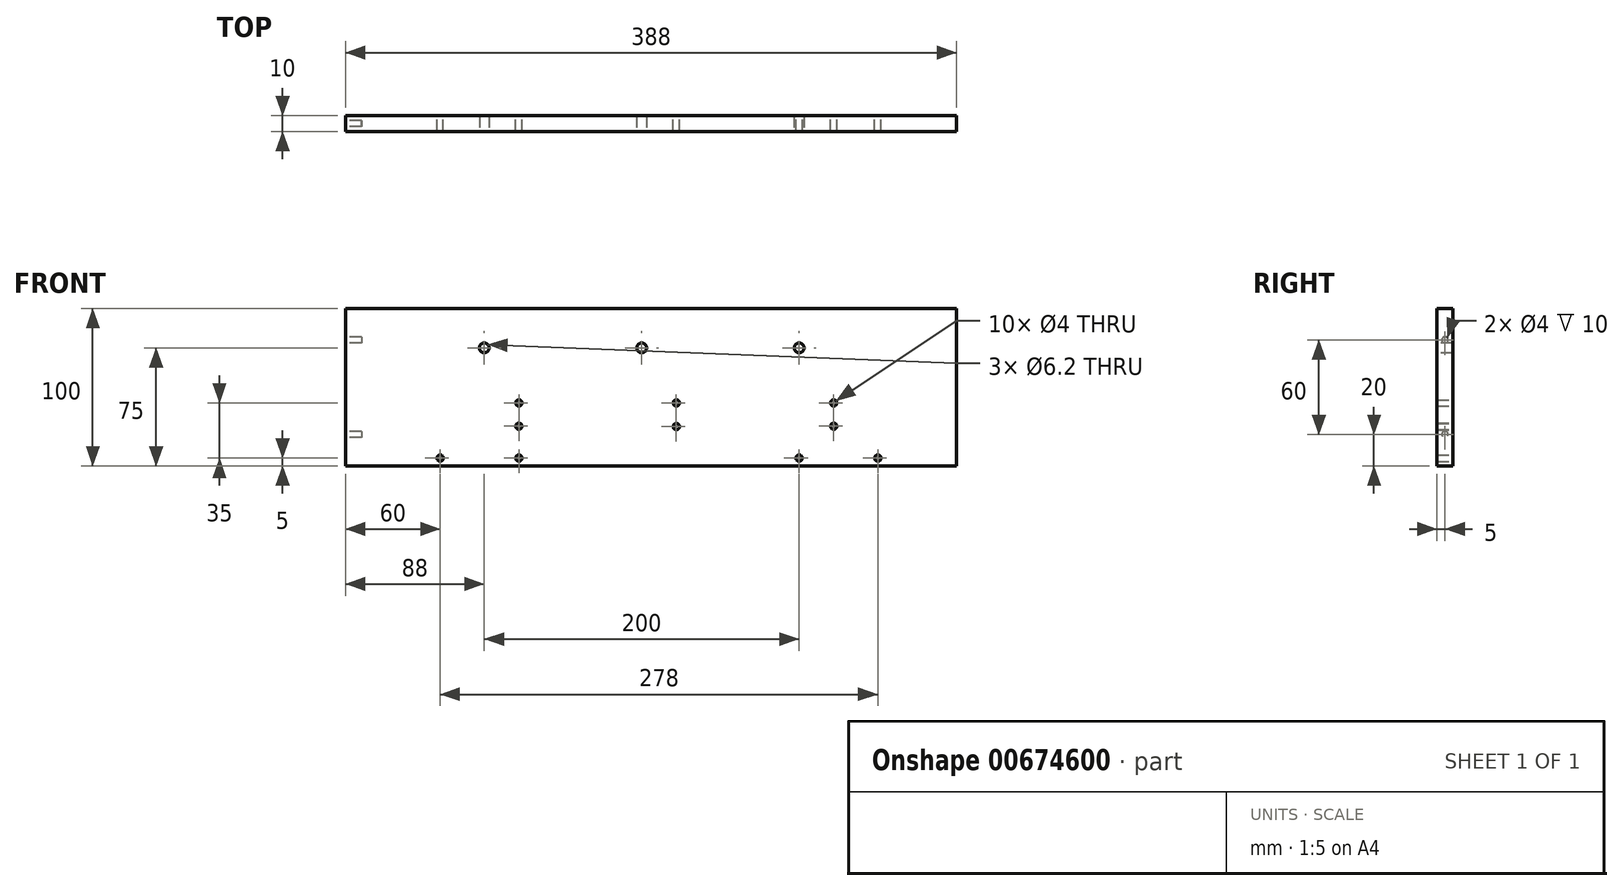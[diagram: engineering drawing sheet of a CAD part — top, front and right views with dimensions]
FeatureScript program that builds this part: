
annotation { "Feature Type Name" : "Feature", "Feature Type Description" : "" }
export const myFeature = defineFeature(function(context is Context, id is Id, definition is map)
    precondition{}
    {
        {
            var Q0;
            Q0=qCreatedBy(makeId("Front.planeOp"),FACE);
            var sketch = newSketch(context, id + "F0", { "sketchPlane" : qUnion([Q0])});
            skLineSegment(sketch, "E0.bottom", {"start": v(194, 50) * mm, "end": v(-194, 50) * mm});
            skLineSegment(sketch, "E0.top", {"start": v(194, -50) * mm, "end": v(-194, -50) * mm});
            skLineSegment(sketch, "E0.left", {"start": v(194, 50) * mm, "end": v(194, -50) * mm});
            skLineSegment(sketch, "E0.right", {"start": v(-194, 50) * mm, "end": v(-194, -50) * mm});
            skPoint(sketch, "E0.middle", {"position": v(0, 0) * mm});
            skCircle(sketch, "E1", {"center": v(144, -45) * mm, "radius": 2 * mm});
            skCircle(sketch, "E2", {"center": v(-134, -45) * mm, "radius": 2 * mm});
            skPoint(sketch, "E3", {"position": v(0, -45) * mm});
            skCircle(sketch, "E4", {"center": v(116, -10) * mm, "radius": 2 * mm});
            skCircle(sketch, "E5", {"center": v(16, -10) * mm, "radius": 2 * mm});
            skCircle(sketch, "E6", {"center": v(-84, -10) * mm, "radius": 2 * mm});
            skLineSegment(sketch, "E7", {"start": v(-84, -10) * mm, "end": v(16, -10) * mm, "construction": true});
            skLineSegment(sketch, "E8", {"start": v(116, -10) * mm, "end": v(16, -10) * mm, "construction": true});
            skCircle(sketch, "E9", {"center": v(-84, -45) * mm, "radius": 2 * mm});
            skCircle(sketch, "E10", {"center": v(94, -45) * mm, "radius": 2 * mm});
            skCircle(sketch, "E11", {"center": v(116, -24.75) * mm, "radius": 2 * mm});
            skCircle(sketch, "E12", {"center": v(16, -25) * mm, "radius": 2 * mm});
            skCircle(sketch, "E13", {"center": v(-84, -24.75) * mm, "radius": 2 * mm});
            skSolve(sketch);
        }
        {
            var Q0;
            Q0=qSketchRegion(id+"F0",true);
            extrude(context, id + "F1", {"entities" : qUnion([Q0]), "depth" : 10 * mm, "offsetDistance" : 25 * mm});
        }
        {
            var Q0;
            Q0=makeQuery(id+"F1.opExtrude","CAP_FACE",FACE,{"disambiguationData":[OSD([sQuery(id+"F0.wireOp",EDGE,"E0.bottom"),sQuery(id+"F0.wireOp",EDGE,"E0.top"),sQuery(id+"F0.wireOp",EDGE,"E0.left"),sQuery(id+"F0.wireOp",EDGE,"E0.right"),sQuery(id+"F0.wireOp",EDGE,"E1"),sQuery(id+"F0.wireOp",EDGE,"E2"),sQuery(id+"F0.wireOp",EDGE,"E4"),sQuery(id+"F0.wireOp",EDGE,"E5"),sQuery(id+"F0.wireOp",EDGE,"E6")])],"isStart":false});
            var sketch = newSketch(context, id + "F2", { "sketchPlane" : qUnion([Q0])});
            skCircle(sketch, "E14", {"center": v(-6, 25) * mm, "radius": 3.1 * mm});
            skCircle(sketch, "E15", {"center": v(94, 25) * mm, "radius": 3.1 * mm});
            skCircle(sketch, "E16", {"center": v(-106, 25) * mm, "radius": 3.1 * mm});
            skSolve(sketch);
        }
        {
            var Q0;
            Q0=qSketchRegion(id+"F2",true);
            extrude(context, id + "F3", {"entities" : qUnion([Q0]), "operationType" : NewBodyOperationType.REMOVE, "oppositeDirection" : true, "depth" : 10 * mm, "offsetDistance" : 25 * mm});
        }
        {
            var Q0;
            Q0=makeQuery(id+"F1.opExtrude","SWEPT_FACE",FACE,{"disambiguationData":[OSD([sQuery(id+"F0.wireOp",EDGE,"E0.right")])]});
            var sketch = newSketch(context, id + "F4", { "sketchPlane" : qUnion([Q0])});
            skCircle(sketch, "E17", {"center": v(5, -30) * mm, "radius": 2 * mm});
            skCircle(sketch, "E18", {"center": v(5, 30) * mm, "radius": 2 * mm});
            skPoint(sketch, "E18.centerSnap0", {"position": v(5, 50) * mm});
            skSolve(sketch);
        }
        {
            var Q0;
            Q0=qSketchRegion(id+"F4",true);
            extrude(context, id + "F5", {"entities" : qUnion([Q0]), "operationType" : NewBodyOperationType.REMOVE, "oppositeDirection" : true, "depth" : 10 * mm, "offsetDistance" : 25 * mm});
        }
    });
